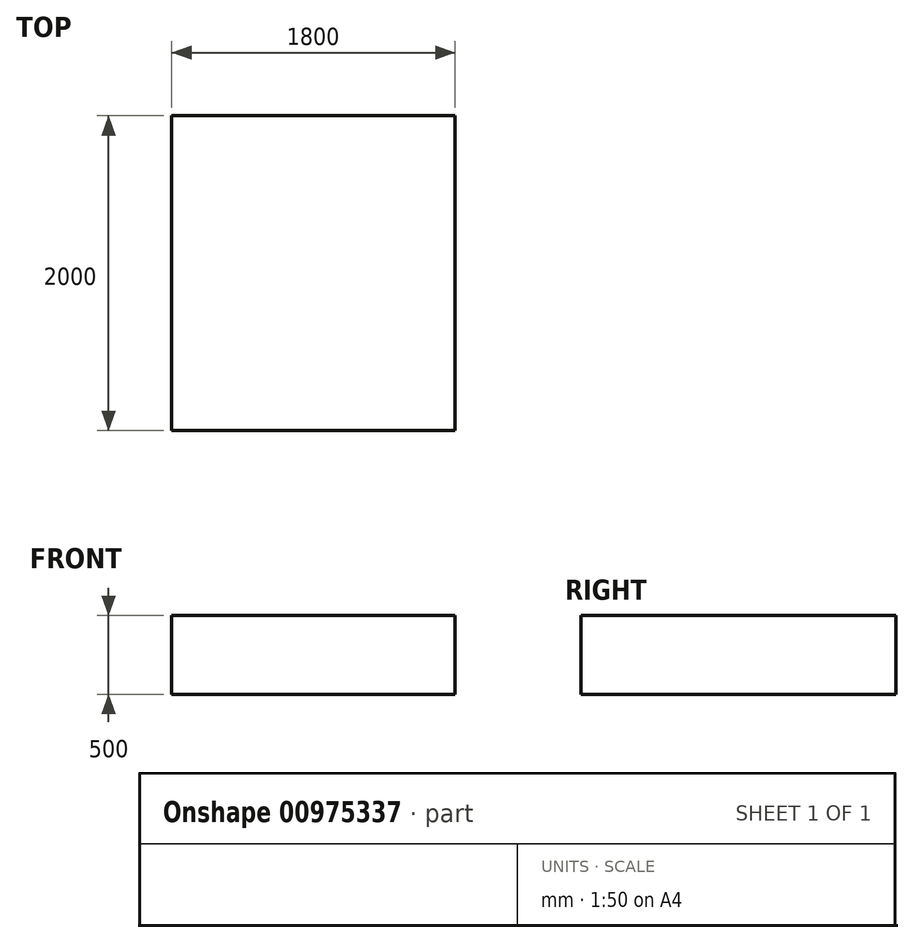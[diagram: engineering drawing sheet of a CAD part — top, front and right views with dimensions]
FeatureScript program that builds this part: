
annotation { "Feature Type Name" : "Feature", "Feature Type Description" : "" }
export const myFeature = defineFeature(function(context is Context, id is Id, definition is map)
    precondition{}
    {
        {
            var Q0;
            Q0=qCreatedBy(makeId("Top.planeOp"),FACE);
            var sketch = newSketch(context, id + "F0", { "sketchPlane" : qUnion([Q0])});
            skLineSegment(sketch, "E0.bottom", {"start": v(-795.5, 2000) * mm, "end": v(1004.5, 2000) * mm});
            skLineSegment(sketch, "E0.top", {"start": v(-795.5, 0) * mm, "end": v(1004.5, 0) * mm});
            skLineSegment(sketch, "E0.left", {"start": v(-795.5, 2000) * mm, "end": v(-795.5, 0) * mm});
            skLineSegment(sketch, "E0.right", {"start": v(1004.5, 2000) * mm, "end": v(1004.5, 0) * mm});
            skSolve(sketch);
        }
        {
            var Q0;
            Q0=makeQuery(id+"F0.imprint","IMPRINT",FACE,{"disambiguationData":[TD([[makeQuery(id+"F0.imprint","IMPRINT",EDGE,{"derivedFrom":sQuery(id+"F0.wireOp",EDGE,"E0.bottom")}),-1.0]])]});
            extrude(context, id + "F1", {"entities" : qUnion([Q0]), "depth" : 500 * mm, "offsetDistance" : 25 * mm});
        }
    });
